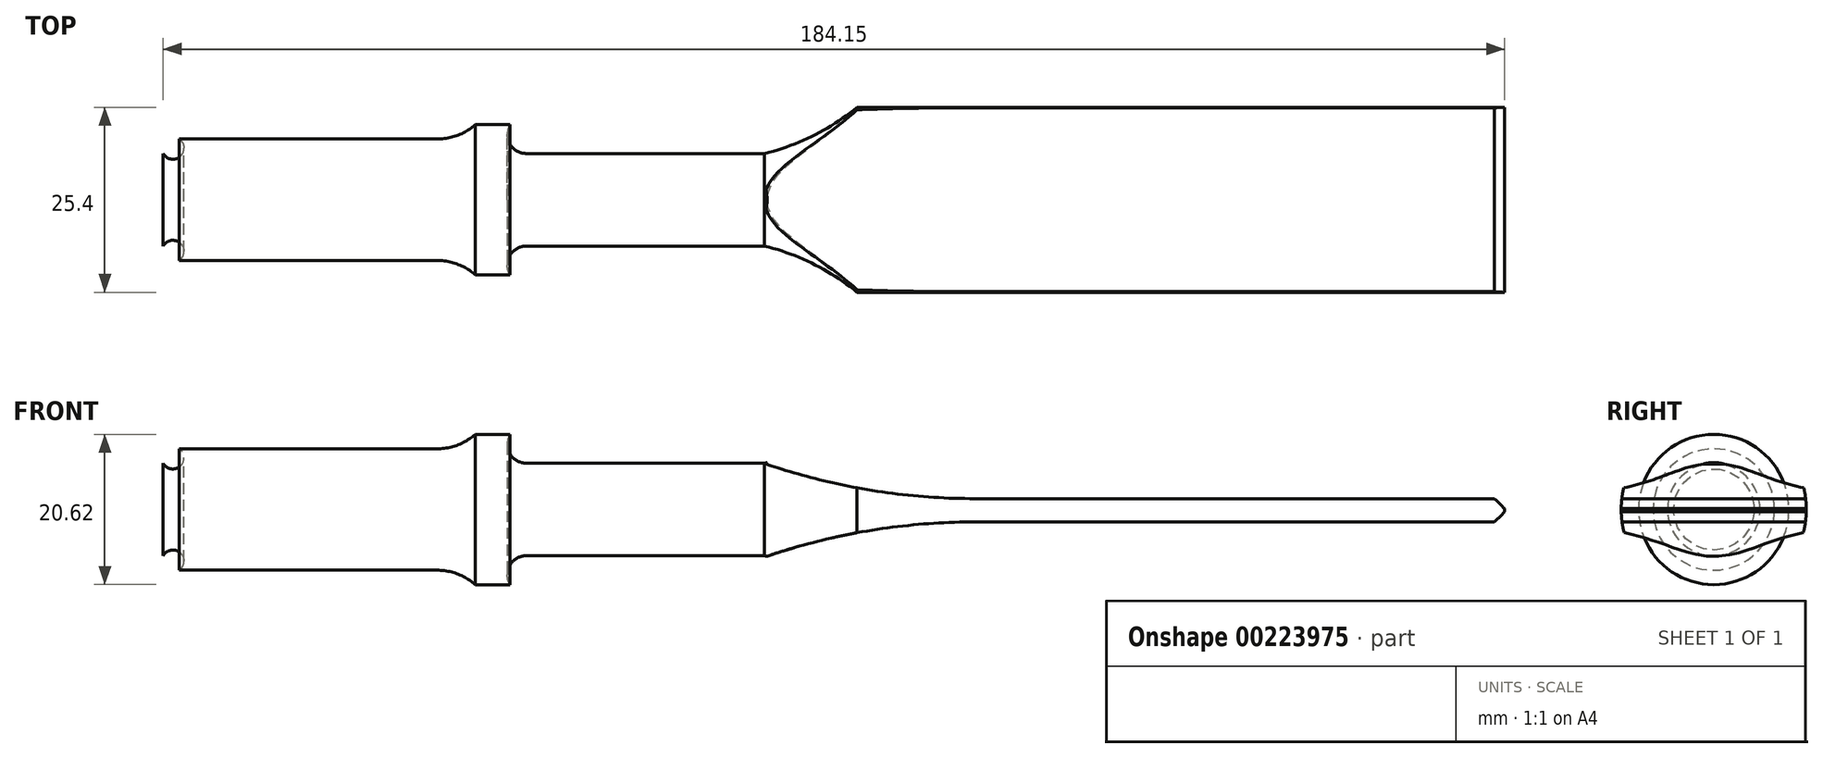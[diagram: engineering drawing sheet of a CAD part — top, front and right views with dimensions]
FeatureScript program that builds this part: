
annotation { "Feature Type Name" : "Feature", "Feature Type Description" : "" }
export const myFeature = defineFeature(function(context is Context, id is Id, definition is map)
    precondition{}
    {
        {
            var Q0;
            Q0=qCreatedBy(makeId("Front.planeOp"),FACE);
            var sketch = newSketch(context, id + "F0", { "sketchPlane" : qUnion([Q0])});
            skLineSegment(sketch, "E0", {"start": v(-95.25, -12.72) * mm, "end": v(88.9, -12.72) * mm});
            skLineSegment(sketch, "E1", {"start": v(88.9, -12.72) * mm, "end": v(88.9, -0.02) * mm});
            skLineSegment(sketch, "E2", {"start": v(88.9, -0.02) * mm, "end": v(0, -0.02) * mm});
            skArc(sketch, "E3", {"start": v(-12.7, -6.37) * mm, "mid": v(-6, -3.92) * mm, "end": v(0, -0.02) * mm});
            skLineSegment(sketch, "E4", {"start": v(-95.25, -12.72) * mm, "end": v(-95.25, -6.37) * mm});
            skArc(sketch, "E5", {"start": v(-95.25, -6.37) * mm, "mid": v(-92.9, -6.77) * mm, "end": v(-93.04, -4.39) * mm});
            skLineSegment(sketch, "E6", {"start": v(-93.04, -4.39) * mm, "end": v(-57.64, -4.39) * mm});
            skArc(sketch, "E7", {"start": v(-57.64, -4.39) * mm, "mid": v(-54.84, -3.88) * mm, "end": v(-52.4, -2.4) * mm});
            skLineSegment(sketch, "E8", {"start": v(-52.4, -2.4) * mm, "end": v(-47.65, -2.4) * mm});
            skLineSegment(sketch, "E9", {"start": v(-12.7, -6.37) * mm, "end": v(-45.39, -6.37) * mm});
            skArc(sketch, "E10", {"start": v(-47.65, -2.4) * mm, "mid": v(-47.67, -5.05) * mm, "end": v(-45.39, -6.37) * mm});
            skSolve(sketch);
        }
        {
            var Q0;
            Q0=makeQuery(id+"F0.imprint","IMPRINT",FACE,{"disambiguationData":[TD([[makeQuery(id+"F0.imprint","IMPRINT",EDGE,{"derivedFrom":sQuery(id+"F0.wireOp",EDGE,"E0")}),1.0]])]});
            var Q1;
            Q1=sQuery(id+"F0.wireOp",EDGE,"E0");
            revolve(context, id + "F1", {"entities" : qUnion([Q0]), "axis" : qUnion([Q1]), "revolveType" : RevolveType.FULL});
        }
        {
            var Q0;
            Q0=qCreatedBy(makeId("Front.planeOp"),FACE);
            var sketch = newSketch(context, id + "F2", { "sketchPlane" : qUnion([Q0])});
            skLineSegment(sketch, "E11", {"start": v(0, 0) * mm, "end": v(0, -25.66) * mm, "construction": true});
            skLineSegment(sketch, "E12", {"start": v(0, -12.83) * mm, "end": v(89.12, -12.83) * mm, "construction": true});
            skLineSegment(sketch, "E13.0", {"start": v(16.19, -11.23) * mm, "end": v(87.52, -11.23) * mm});
            skArc(sketch, "E14", {"start": v(-12.48, -6.48) * mm, "mid": v(1.66, -10.04) * mm, "end": v(16.19, -11.23) * mm});
            skPoint(sketch, "E15", {"position": v(-12.48, -6.48) * mm});
            skLineSegment(sketch, "E16", {"start": v(89.12, -12.83) * mm, "end": v(87.52, -11.23) * mm});
            skPoint(sketch, "E17.start.orphan", {"position": v(89.12, -25.66) * mm});
            skPoint(sketch, "E18.start.orphan", {"position": v(89.12, 0) * mm});
            skLineSegment(sketch, "E19", {"start": v(-12.48, -6.48) * mm, "end": v(7.2, 21.5) * mm});
            skLineSegment(sketch, "E20", {"start": v(7.2, 21.5) * mm, "end": v(96.56, 18.12) * mm});
            skLineSegment(sketch, "E21", {"start": v(96.56, 18.12) * mm, "end": v(89.12, -12.83) * mm});
            skLineSegment(sketch, "E22.MirrorCS", {"start": v(16.19, -14.43) * mm, "end": v(87.52, -14.43) * mm});
            skArc(sketch, "E23.MirrorCS", {"start": v(-12.48, -19.18) * mm, "mid": v(1.66, -15.63) * mm, "end": v(16.19, -14.43) * mm});
            skLineSegment(sketch, "E24.MirrorCS", {"start": v(89.12, -12.83) * mm, "end": v(87.52, -14.43) * mm});
            skLineSegment(sketch, "E25.MirrorCS", {"start": v(96.56, -43.79) * mm, "end": v(89.12, -12.83) * mm});
            skLineSegment(sketch, "E26.MirrorCS", {"start": v(-12.48, -19.18) * mm, "end": v(7.2, -47.17) * mm});
            skLineSegment(sketch, "E27.MirrorCS", {"start": v(7.2, -47.17) * mm, "end": v(96.56, -43.79) * mm});
            skSolve(sketch);
        }
        {
            var Q0;
            Q0 = qSketchRegion(id + "F2", true);
            extrude(context, id + "F3", {"entities" : qUnion([Q0]), "operationType" : NewBodyOperationType.REMOVE, "oppositeDirection" : true, "depth" : 25.4 * mm});
        }
        {
            var Q0;
            Q0 = qSketchRegion(id + "F2", true);
            extrude(context, id + "F4", {"entities" : qUnion([Q0]), "operationType" : NewBodyOperationType.REMOVE, "depth" : 25.4 * mm});
        }
    });
